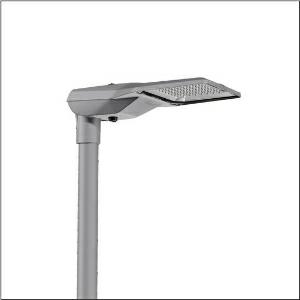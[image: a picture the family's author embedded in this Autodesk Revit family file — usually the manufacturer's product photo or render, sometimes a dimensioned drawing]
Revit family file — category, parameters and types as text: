
# Revit family: streetlight_sl_21_midi___p0_8a_5xe3u33t08lb_3dc7
name_source: partatom
category: Lighting Fixtures
units: mm (PartAtom-declared; Revit-internal decimal feet)

## family parameters
Cut with Voids When Loaded = No
Host = Face
Light Source = No
Part Type = Normal
Room Calculation Point = No
Round Connector Dimension = Use Diameter
Shared = No

## types (1)
- --- (1 x LED, 14470 lm, 99.6 W, 3000K)
    Apparent Load = 100 VA
    CIE Flux Codes = 33 69 96 100 100
    Color Rendering = 70
    Color Temperature = 3000K
    Default Elevation = 1800 mm
    Description = Streetlight SL 21 midi, mast luminaire, primary light control with lens, of PMMA, primary optical cover: cover, of toughened safety glass, transparent, light distribution: P0.8a, light emission: direct distribution, primary light characteristic: asymmetric, installation type: post-top, side-entry, LED, High Power LED, rated luminous flux: 14.470lm, luminous efficacy: 145lm/W, light colour: 730, colour temperature: 3000K, control gear: D4i, control: pre-setting: logarithmic dimming characteristic, flexible luminous flux parameterisation, time-dependent luminous flux control, constant luminous flux control, overheat protection, mains connection: 230..240V, AC, 50/60Hz, start of lifetime: 100W, end of service life: 102W, reduction: 46W, luminaire housing, of diecast aluminium, powder-coated, Siteco® metallic grey (DB 702S), corrosivity category C5 mid according to DIN EN ISO 12944, multi-level sealing system, sealing non-destructively replaceable, inclination adjustable: 0°, 5°, 10°, 15°, please order mast flange separately, length: 644mm, width: 335mm, height: 110mm, mast flange for spigot size: 42mm (side-entry): 5XC10008XM4, 60/48mm (side-entry/post-top): 5XC10108XM2, 76/60mm (side-entry/post-top): 5XC10108XM1, mounting height: 4..8m, Smart Interface below and above, protection rating (complete): IP66, insulation class (complete): insulation class II (safety insulation), certification: CE, ENEC, ENEC+, VDE, impact resistance: IK10, permissible operating ambient temperature for outdoor applications: -40..+50°C, standard-compliant lighting for roads and squares, packaging unit: 1 piece

Light Distribution: P0.8a
    Height = 111 mm
    Lamp = 1 x LED
    Lamp Light Flux = 14470 lm
    Lamp Power = 99.6 W
    Lamp count = 1
    Length = 644 mm
    Luminous efficacy = 145 lm/W
    Manufacturer = Siteco
    ModVariant = No
    Model = 5XE3U33T08LB
    Number of Poles = 1
    OnlyDefault = Yes
    Power Factor = 1
    Product Name = Streetlight SL 21 midi | P0.8a
    Product group = mast luminaire | pylon top
    ProductGroupID = 6100
    Protection Class = Protection class II
    Protection Degree = IP 66
    RLX_Detail_Level = 1
    RLX_Emergency_Light_Flux = 0 lm
    RLX_Emergency_Type = 0
    RLX_Emergency_Type_DB = No
    RlxData = <blob elided: 26749 chars, md5=86ecdfb6>
    Socket = socket
    Standby Power = 0 W
    System Light Flux = 14470 lm
    System Power = 100 W
    Type Comments = factory setting: luminous flux: 100 % | dim-lin: 254 | 1020 mA
    Type Image = l_1004304.jpg
    URL = http://relux.com
    VarID = @adj_013395
    Voltage = 0 V
    Weight = 0.00 kg
    Width = 336 mm

## geometry (parser evidence)
native form markers: Blend x4, Sweep x11
no freeform markers — native parametric forms only
